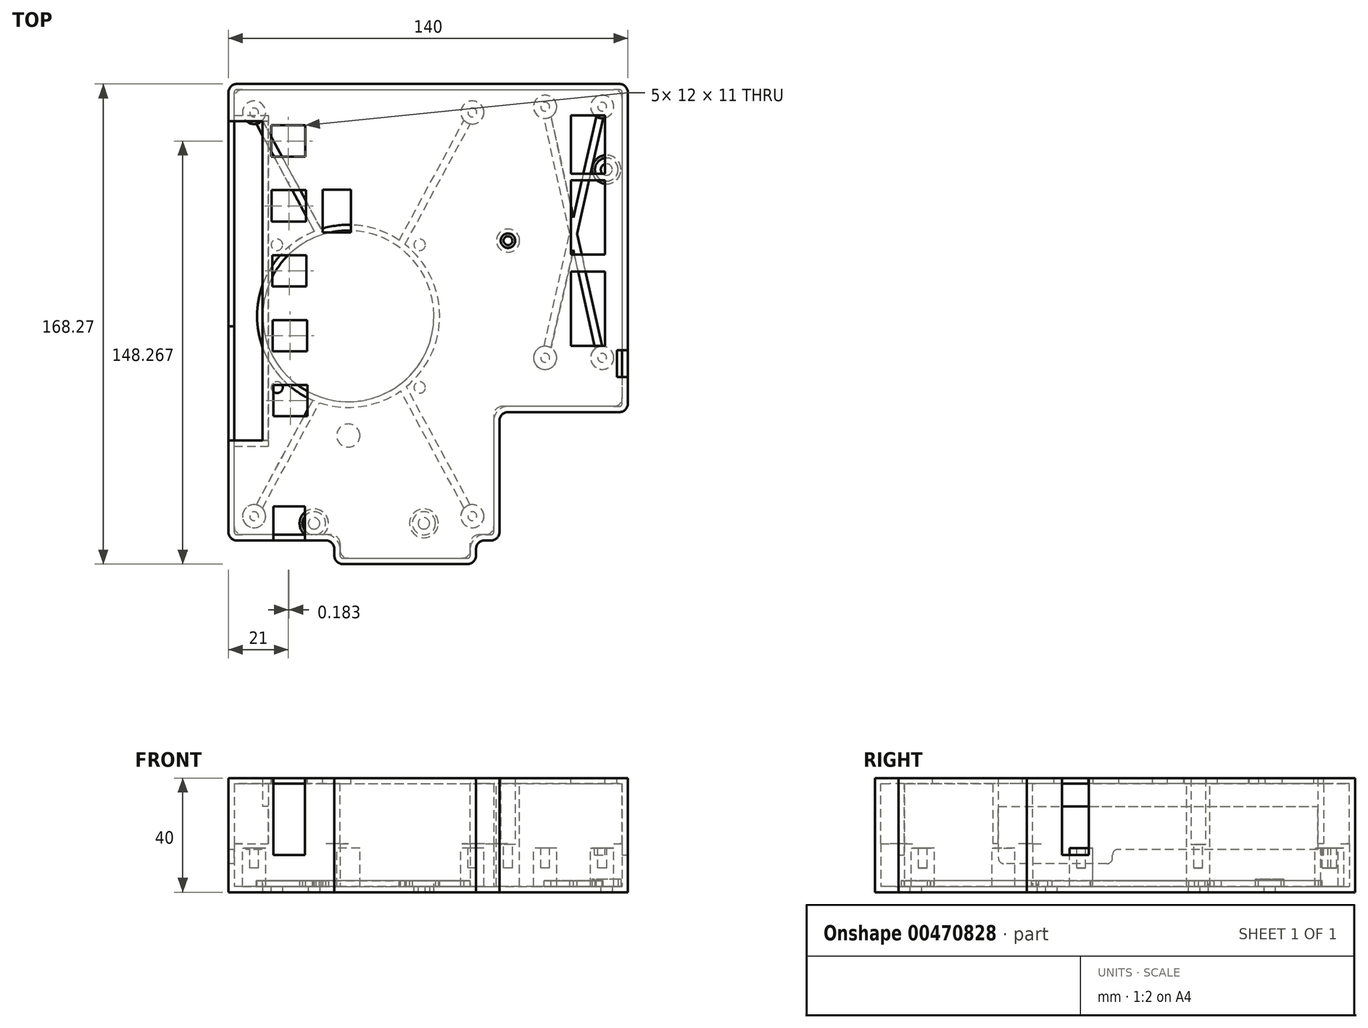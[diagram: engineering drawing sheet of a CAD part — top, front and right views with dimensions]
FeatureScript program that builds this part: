
annotation { "Feature Type Name" : "Feature", "Feature Type Description" : "" }
export const myFeature = defineFeature(function(context is Context, id is Id, definition is map)
    precondition{}
    {
        {
            assignVariable(context, id + "F0", {"name" : "BottomShellHeight", "anyValue" : 15 * mm});
        }
        {
            assignVariable(context, id + "F1", {"name" : "BoardThickness", "anyValue" : 1.6 * mm});
        }
        {
            assignVariable(context, id + "F2", {"name" : "TopShellHeight", "anyValue" : 23 * mm});
        }
        {
            var Q0;
            Q0=qCreatedBy(makeId("Top.planeOp"),FACE);
            var sketch = newSketch(context, id + "F3", { "sketchPlane" : qUnion([Q0])});
            skLineSegment(sketch, "E0", {"start": v(-42.03, -43.02) * mm, "end": v(-42.03, 116.98) * mm});
            skLineSegment(sketch, "E1", {"start": v(-42.03, 116.98) * mm, "end": v(97.97, 116.98) * mm});
            skLineSegment(sketch, "E2", {"start": v(97.97, 116.98) * mm, "end": v(97.97, 1.98) * mm});
            skLineSegment(sketch, "E3", {"start": v(97.97, 1.98) * mm, "end": v(52.97, 1.98) * mm});
            skLineSegment(sketch, "E4", {"start": v(52.97, 1.98) * mm, "end": v(52.97, -43.02) * mm});
            skLineSegment(sketch, "E5", {"start": v(52.97, -43.02) * mm, "end": v(-42.03, -43.02) * mm});
            skCircle(sketch, "E6", {"center": v(90.47, 86.98) * mm, "radius": 2.5 * mm});
            skCircle(sketch, "E7", {"center": v(90.47, 26.98) * mm, "radius": 2.5 * mm});
            skCircle(sketch, "E8", {"center": v(26.47, -37.02) * mm, "radius": 2.5 * mm});
            skCircle(sketch, "E9", {"center": v(-12.03, -37.02) * mm, "radius": 2.5 * mm});
            skLineSegment(sketch, "E10", {"start": v(-4.91, -43.02) * mm, "end": v(-4.91, -51.29) * mm});
            skLineSegment(sketch, "E11", {"start": v(-4.91, -51.29) * mm, "end": v(44.74, -51.29) * mm});
            skLineSegment(sketch, "E12", {"start": v(44.74, -51.29) * mm, "end": v(44.74, -43.02) * mm});
            skSolve(sketch);
        }
        {
            var Q0;
            Q0=makeQuery(id+"F3.imprint","IMPRINT",FACE,{"disambiguationData":[TD([[makeQuery(id+"F3.imprint","IMPRINT",EDGE,{"derivedFrom":sQuery(id+"F3.wireOp",EDGE,"E0")}),-1.0]])]});
            var Q1;
            Q1=makeQuery(id+"F3.imprint","IMPRINT",FACE,{"disambiguationData":[TD([[makeQuery(id+"F3.imprint","IMPRINT",EDGE,{"derivedFrom":sQuery(id+"F3.wireOp",EDGE,"E8")}),1.0]])]});
            var Q2;
            Q2=makeQuery(id+"F3.imprint","IMPRINT",FACE,{"disambiguationData":[TD([[makeQuery(id+"F3.imprint","IMPRINT",EDGE,{"derivedFrom":sQuery(id+"F3.wireOp",EDGE,"E9")}),1.0]])]});
            var Q3;
            Q3=makeQuery(id+"F3.imprint","IMPRINT",FACE,{"disambiguationData":[TD([[makeQuery(id+"F3.imprint","IMPRINT",EDGE,{"derivedFrom":sQuery(id+"F3.wireOp",EDGE,"E6")}),1.0]])]});
            var Q4;
            Q4=makeQuery(id+"F3.imprint","IMPRINT",FACE,{"disambiguationData":[TD([[makeQuery(id+"F3.imprint","IMPRINT",EDGE,{"derivedFrom":sQuery(id+"F3.wireOp",EDGE,"E7")}),1.0]])]});
            var Q5;
            {var subQ1=sQuery(id+"F3.wireOp",EDGE,"E10");Q5=makeQuery(id+"F3.imprint","IMPRINT",FACE,{"disambiguationData":[TD([[makeQuery(id+"F3.imprint","IMPRINT",EDGE,{"derivedFrom":subQ1}),1.0]])]});}
            extrude(context, id + "F4", {"entities" : qUnion([Q0, Q1, Q2, Q3, Q4, Q5]), "depth" : getVariable(context, 'BottomShellHeight')});
        }
        {
            var Q0;
            Q0=makeQuery(id+"F4.opExtrude","CAP_FACE",FACE,{"disambiguationData":[OSD([sQuery(id+"F3.wireOp",EDGE,"E0"),sQuery(id+"F3.wireOp",EDGE,"E1"),sQuery(id+"F3.wireOp",EDGE,"E2"),sQuery(id+"F3.wireOp",EDGE,"E3"),sQuery(id+"F3.wireOp",EDGE,"E4"),sQuery(id+"F3.wireOp",EDGE,"E5")])],"isStart":false});
            shell(context, id + "F5", {"entities" : qUnion([Q0]), "thickness" : 2 * mm});
        }
        {
            var Q0;
            Q0=sQuery(id+"F3.wireOp",VERTEX,"E9.center");
            var Q1;
            Q1=sQuery(id+"F3.wireOp",VERTEX,"E8.center");
            var Q2;
            Q2=sQuery(id+"F3.wireOp",VERTEX,"E6.center");
            var Q3;
            Q3=makeQuery(id+"F4.opExtrude","SWEPT_BODY",BODY,{"disambiguationData":[OSD([sQuery(id+"F3.wireOp",EDGE,"E0"),sQuery(id+"F3.wireOp",EDGE,"E1"),sQuery(id+"F3.wireOp",EDGE,"E2"),sQuery(id+"F3.wireOp",EDGE,"E3"),sQuery(id+"F3.wireOp",EDGE,"E4"),sQuery(id+"F3.wireOp",EDGE,"E5")])]});
            hole(context, id + "F6", {"style" : HoleStyle.SIMPLE, "holeDiameter" : 4 * mm, "endStyle" : HoleEndStyle.THROUGH, "oppositeDirection" : true, "locations" : qUnion([Q0, Q1, Q2]), "scope" : qUnion([Q3])});
        }
        {
            var Q0;
            Q0=makeQuery(id+"F5.opShell","OFFSET_FACE",FACE,{"disambiguationData":[OSD([sQuery(id+"F3.wireOp",EDGE,"E0"),sQuery(id+"F3.wireOp",EDGE,"E1"),sQuery(id+"F3.wireOp",EDGE,"E2"),sQuery(id+"F3.wireOp",EDGE,"E3"),sQuery(id+"F3.wireOp",EDGE,"E4"),sQuery(id+"F3.wireOp",EDGE,"E5")])]});
            var sketch = newSketch(context, id + "F7", { "sketchPlane" : qUnion([Q0])});
            skCircle(sketch, "E13", {"center": v(-12.03, -37.02) * mm, "radius": 4.05 * mm});
            skCircle(sketch, "E14", {"center": v(26.47, -37.02) * mm, "radius": 4.05 * mm});
            skCircle(sketch, "E15", {"center": v(90.47, 86.98) * mm, "radius": 4.05 * mm});
            skCircle(sketch, "E16", {"center": v(90.47, 86.98) * mm, "radius": 5.05 * mm});
            skCircle(sketch, "E17", {"center": v(26.47, -37.02) * mm, "radius": 5.05 * mm});
            skCircle(sketch, "E18", {"center": v(-12.03, -37.02) * mm, "radius": 5.05 * mm});
            skLineSegment(sketch, "E19.rect.bottom", {"start": v(25, 10.6) * mm, "end": v(-25, 10.6) * mm, "construction": true});
            skLineSegment(sketch, "E19.rect.top", {"start": v(25, 60.6) * mm, "end": v(-25, 60.6) * mm, "construction": true});
            skLineSegment(sketch, "E19.rect.left", {"start": v(25, 10.6) * mm, "end": v(25, 60.6) * mm, "construction": true});
            skLineSegment(sketch, "E19.rect.right", {"start": v(-25, 10.6) * mm, "end": v(-25, 60.6) * mm, "construction": true});
            skPoint(sketch, "E19.rect.middle", {"position": v(0, 35.6) * mm});
            skCircle(sketch, "E20", {"center": v(0, 35.6) * mm, "radius": 30 * mm});
            skSolve(sketch);
        }
        {
            var Q0;
            Q0=makeQuery(id+"F7.imprint","IMPRINT",FACE,{"disambiguationData":[TD([[makeQuery(id+"F7.imprint","IMPRINT",EDGE,{"derivedFrom":sQuery(id+"F7.wireOp",EDGE,"E15")}),-1.0]])]});
            extrude(context, id + "F8", {"entities" : qUnion([Q0]), "operationType" : NewBodyOperationType.ADD, "depth" : 2.5 * mm});
        }
        {
            var Q0;
            Q0=makeQuery(id+"F7.imprint","IMPRINT",FACE,{"disambiguationData":[TD([[makeQuery(id+"F7.imprint","IMPRINT",EDGE,{"derivedFrom":sQuery(id+"F7.wireOp",EDGE,"E16")}),-1.0]])]});
            cPlane(context, id + "F9", {"entities" : qUnion([Q0]), "cplaneType" : CPlaneType.OFFSET, "offset" : getVariable(context, 'BottomShellHeight') - getVariable(context, 'BoardThickness'), "width" : 150 * mm, "height" : 150 * mm});
        }
        {
            var Q0;
            Q0=qCreatedBy(id+"F9.planeOp",FACE);
            var sketch = newSketch(context, id + "F10", { "sketchPlane" : qUnion([Q0])});
            skCircle(sketch, "E21", {"center": v(-33.03, 106.98) * mm, "radius": 4.05 * mm});
            skCircle(sketch, "E22", {"center": v(43.47, 106.98) * mm, "radius": 4.05 * mm});
            skCircle(sketch, "E23", {"center": v(68.97, 108.98) * mm, "radius": 4.05 * mm});
            skCircle(sketch, "E24", {"center": v(88.97, 108.98) * mm, "radius": 4.05 * mm});
            skCircle(sketch, "E25", {"center": v(68.97, 20.98) * mm, "radius": 4.05 * mm});
            skCircle(sketch, "E26", {"center": v(-33.03, -34.52) * mm, "radius": 4.05 * mm});
            skCircle(sketch, "E27", {"center": v(43.47, -34.52) * mm, "radius": 4.05 * mm});
            skCircle(sketch, "E28", {"center": v(88.97, 20.98) * mm, "radius": 4.05 * mm});
            skCircle(sketch, "E29", {"center": v(0, -6.24) * mm, "radius": 4.05 * mm});
            skCircle(sketch, "E30", {"center": v(55.94, 62.04) * mm, "radius": 4.05 * mm});
            skSolve(sketch);
        }
        {
            var Q0;
            Q0=qSketchRegion(id+"F10",true);
            extrude(context, id + "F11", {"entities" : qUnion([Q0]), "operationType" : NewBodyOperationType.ADD, "endBound" : BoundingType.UP_TO_NEXT, "oppositeDirection" : true, "depth" : 25 * mm});
        }
        {
            var Q0;
            Q0=qCreatedBy(makeId("Top.planeOp"),FACE);
            cPlane(context, id + "F12", {"entities" : qUnion([Q0]), "cplaneType" : CPlaneType.OFFSET, "offset" : 4 * mm, "width" : 150 * mm, "height" : 150 * mm});
        }
        {
            var Q0;
            Q0=qCreatedBy(id+"F12.planeOp",FACE);
            var sketch = newSketch(context, id + "F13", { "sketchPlane" : qUnion([Q0])});
            skCircle(sketch, "E31.0", {"center": v(-33.03, 106.98) * mm, "radius": 4.05 * mm, "construction": true});
            skCircle(sketch, "E31.1", {"center": v(43.47, 106.98) * mm, "radius": 4.05 * mm, "construction": true});
            skCircle(sketch, "E31.2", {"center": v(68.97, 108.98) * mm, "radius": 4.05 * mm, "construction": true});
            skCircle(sketch, "E31.3", {"center": v(88.97, 108.98) * mm, "radius": 4.05 * mm, "construction": true});
            skCircle(sketch, "E31.5", {"center": v(68.97, 20.98) * mm, "radius": 4.05 * mm, "construction": true});
            skCircle(sketch, "E31.6", {"center": v(43.47, -34.52) * mm, "radius": 4.05 * mm, "construction": true});
            skCircle(sketch, "E31.7", {"center": v(-33.03, -34.52) * mm, "radius": 4.05 * mm, "construction": true});
            skLineSegment(sketch, "E32", {"start": v(-33.03, 106.98) * mm, "end": v(43.47, -34.52) * mm, "construction": true});
            skLineSegment(sketch, "E33", {"start": v(68.97, 108.98) * mm, "end": v(88.97, 18.98) * mm, "construction": true});
            skLineSegment(sketch, "E34", {"start": v(88.97, 108.98) * mm, "end": v(68.97, 20.98) * mm, "construction": true});
            skLineSegment(sketch, "E35", {"start": v(43.47, 106.98) * mm, "end": v(-33.03, -34.52) * mm, "construction": true});
            skArc(sketch, "E36.0.startCap", {"start": v(-34.13, 106.38) * mm, "mid": v(-33.62, 108.08) * mm, "end": v(-31.93, 107.57) * mm});
            skArc(sketch, "E36.0.endCap", {"start": v(44.57, -33.93) * mm, "mid": v(44.06, -35.62) * mm, "end": v(42.37, -35.12) * mm});
            skLineSegment(sketch, "E36.0.left", {"start": v(-31.93, 107.57) * mm, "end": v(44.57, -33.93) * mm});
            skLineSegment(sketch, "E36.0.right", {"start": v(-34.13, 106.38) * mm, "end": v(42.37, -35.12) * mm});
            skArc(sketch, "E36.1.startCap", {"start": v(42.37, 107.57) * mm, "mid": v(44.06, 108.08) * mm, "end": v(44.57, 106.38) * mm});
            skArc(sketch, "E36.1.endCap", {"start": v(-31.93, -35.12) * mm, "mid": v(-33.62, -35.62) * mm, "end": v(-34.13, -33.93) * mm});
            skLineSegment(sketch, "E36.1.left", {"start": v(44.57, 106.38) * mm, "end": v(-31.93, -35.12) * mm});
            skLineSegment(sketch, "E36.1.right", {"start": v(42.37, 107.57) * mm, "end": v(-34.13, -33.93) * mm});
            skArc(sketch, "E36.2.startCap", {"start": v(42.27, 106.64) * mm, "mid": v(43.13, 108.18) * mm, "end": v(44.67, 107.32) * mm});
            skArc(sketch, "E36.2.endCap", {"start": v(70.17, 21.32) * mm, "mid": v(69.3, 19.77) * mm, "end": v(67.77, 20.64) * mm});
            skArc(sketch, "E36.3.startCap", {"start": v(44.7, -34.74) * mm, "mid": v(43.25, -35.75) * mm, "end": v(42.24, -34.3) * mm});
            skArc(sketch, "E36.3.endCap", {"start": v(67.74, 109.2) * mm, "mid": v(69.19, 110.2) * mm, "end": v(70.2, 108.76) * mm});
            skArc(sketch, "E36.4.startCap", {"start": v(67.75, 108.7) * mm, "mid": v(68.7, 110.2) * mm, "end": v(70.2, 109.25) * mm});
            skArc(sketch, "E36.4.endCap", {"start": v(90.2, 19.25) * mm, "mid": v(89.24, 17.76) * mm, "end": v(87.75, 18.7) * mm});
            skLineSegment(sketch, "E36.4.left", {"start": v(70.2, 109.25) * mm, "end": v(90.2, 19.25) * mm});
            skLineSegment(sketch, "E36.4.right", {"start": v(67.75, 108.7) * mm, "end": v(87.75, 18.7) * mm});
            skArc(sketch, "E36.5.startCap", {"start": v(87.75, 109.25) * mm, "mid": v(89.25, 110.2) * mm, "end": v(90.19, 108.7) * mm});
            skArc(sketch, "E36.5.endCap", {"start": v(70.19, 20.7) * mm, "mid": v(68.7, 19.76) * mm, "end": v(67.75, 21.25) * mm});
            skLineSegment(sketch, "E36.5.left", {"start": v(90.19, 108.7) * mm, "end": v(70.19, 20.7) * mm});
            skLineSegment(sketch, "E36.5.right", {"start": v(87.75, 109.25) * mm, "end": v(67.75, 21.25) * mm});
            skCircle(sketch, "E37.0", {"center": v(88.97, 20.98) * mm, "radius": 4.05 * mm});
            skCircle(sketch, "E38.0", {"center": v(0, 35.6) * mm, "radius": 32 * mm});
            skSolve(sketch);
        }
        {
            var Q0;
            Q0=qSketchRegion(id+"F13",true);
            var Q1;
            Q1=makeQuery(id+"F5.opShell","OFFSET_FACE",FACE,{"disambiguationData":[OSD([sQuery(id+"F3.wireOp",EDGE,"E0"),sQuery(id+"F3.wireOp",EDGE,"E1"),sQuery(id+"F3.wireOp",EDGE,"E2"),sQuery(id+"F3.wireOp",EDGE,"E3"),sQuery(id+"F3.wireOp",EDGE,"E4"),sQuery(id+"F3.wireOp",EDGE,"E5")])]});
            extrude(context, id + "F14", {"entities" : qUnion([Q0]), "operationType" : NewBodyOperationType.ADD, "endBound" : BoundingType.UP_TO_SURFACE, "oppositeDirection" : true, "endBoundEntityFace" : qUnion([Q1]), "depth" : 25 * mm});
        }
        {
            var Q0;
            Q0=makeQuery(id+"F7.imprint","IMPRINT",FACE,{"disambiguationData":[TD([[makeQuery(id+"F7.imprint","IMPRINT",EDGE,{"derivedFrom":sQuery(id+"F7.wireOp",EDGE,"E20")}),1.0]])]});
            extrude(context, id + "F15", {"entities" : qUnion([Q0]), "operationType" : NewBodyOperationType.REMOVE, "endBound" : BoundingType.SYMMETRIC, "oppositeDirection" : true, "depth" : 5 * mm});
        }
        {
            var Q0;
            Q0=makeQuery(id+"F4.opExtrude","SWEPT_EDGE",EDGE,{"disambiguationData":[OSD([sQuery(id+"F3.wireOp",EDGE,"E0"),sQuery(id+"F3.wireOp",EDGE,"E5")])]});
            var Q1;
            Q1=makeQuery(id+"F4.opExtrude","SWEPT_EDGE",EDGE,{"disambiguationData":[OSD([sQuery(id+"F3.wireOp",EDGE,"E4"),sQuery(id+"F3.wireOp",EDGE,"E5")])]});
            var Q2;
            Q2=makeQuery(id+"F4.opExtrude","SWEPT_EDGE",EDGE,{"disambiguationData":[OSD([sQuery(id+"F3.wireOp",EDGE,"E3"),sQuery(id+"F3.wireOp",EDGE,"E4")])]});
            var Q3;
            Q3=makeQuery(id+"F4.opExtrude","SWEPT_EDGE",EDGE,{"disambiguationData":[OSD([sQuery(id+"F3.wireOp",EDGE,"E2"),sQuery(id+"F3.wireOp",EDGE,"E3")])]});
            var Q4;
            Q4=makeQuery(id+"F4.opExtrude","SWEPT_EDGE",EDGE,{"disambiguationData":[OSD([sQuery(id+"F3.wireOp",EDGE,"E1"),sQuery(id+"F3.wireOp",EDGE,"E2")])]});
            var Q5;
            Q5=makeQuery(id+"F4.opExtrude","SWEPT_EDGE",EDGE,{"disambiguationData":[OSD([sQuery(id+"F3.wireOp",EDGE,"E0"),sQuery(id+"F3.wireOp",EDGE,"E1")])]});
            var Q6;
            Q6=makeQuery(id+"F5.opShell","OFFSET_EDGE",EDGE,{"disambiguationData":[OSD([sQuery(id+"F3.wireOp",EDGE,"E0"),sQuery(id+"F3.wireOp",EDGE,"E5")])]});
            var Q7;
            Q7=makeQuery(id+"F5.opShell","OFFSET_EDGE",EDGE,{"disambiguationData":[OSD([sQuery(id+"F3.wireOp",EDGE,"E0"),sQuery(id+"F3.wireOp",EDGE,"E1")])]});
            var Q8;
            Q8=makeQuery(id+"F5.opShell","OFFSET_EDGE",EDGE,{"disambiguationData":[OSD([sQuery(id+"F3.wireOp",EDGE,"E1"),sQuery(id+"F3.wireOp",EDGE,"E2")])]});
            var Q9;
            Q9=makeQuery(id+"F5.opShell","OFFSET_EDGE",EDGE,{"disambiguationData":[OSD([sQuery(id+"F3.wireOp",EDGE,"E4"),sQuery(id+"F3.wireOp",EDGE,"E5")])]});
            var Q10;
            Q10=makeQuery(id+"F5.opShell","OFFSET_EDGE",EDGE,{"disambiguationData":[OSD([sQuery(id+"F3.wireOp",EDGE,"E3"),sQuery(id+"F3.wireOp",EDGE,"E4")])]});
            var Q11;
            Q11=makeQuery(id+"F5.opShell","OFFSET_EDGE",EDGE,{"disambiguationData":[OSD([sQuery(id+"F3.wireOp",EDGE,"E2"),sQuery(id+"F3.wireOp",EDGE,"E3")])]});
            var Q12;
            Q12=makeQuery(id+"F4.opExtrude","SWEPT_EDGE",EDGE,{"disambiguationData":[OSD([sQuery(id+"F3.wireOp",EDGE,"E10"),sQuery(id+"F3.wireOp",EDGE,"E11")])]});
            var Q13;
            Q13=makeQuery(id+"F4.opExtrude","SWEPT_EDGE",EDGE,{"disambiguationData":[OSD([sQuery(id+"F3.wireOp",EDGE,"E11"),sQuery(id+"F3.wireOp",EDGE,"E12")])]});
            var Q14;
            Q14=makeQuery(id+"F5.opShell","OFFSET_EDGE",EDGE,{"disambiguationData":[OSD([sQuery(id+"F3.wireOp",EDGE,"E10"),sQuery(id+"F3.wireOp",EDGE,"E11")])]});
            var Q15;
            Q15=makeQuery(id+"F5.opShell","OFFSET_EDGE",EDGE,{"disambiguationData":[OSD([sQuery(id+"F3.wireOp",EDGE,"E5"),sQuery(id+"F3.wireOp",EDGE,"E10")])]});
            var Q16;
            Q16=makeQuery(id+"F5.opShell","OFFSET_EDGE",EDGE,{"disambiguationData":[OSD([sQuery(id+"F3.wireOp",EDGE,"E5"),sQuery(id+"F3.wireOp",EDGE,"E12")])]});
            var Q17;
            Q17=makeQuery(id+"F5.opShell","OFFSET_EDGE",EDGE,{"disambiguationData":[OSD([sQuery(id+"F3.wireOp",EDGE,"E11"),sQuery(id+"F3.wireOp",EDGE,"E12")])]});
            var Q18;
            Q18=makeQuery(id+"F4.opExtrude","SWEPT_EDGE",EDGE,{"disambiguationData":[OSD([sQuery(id+"F3.wireOp",EDGE,"E5"),sQuery(id+"F3.wireOp",EDGE,"E12")])]});
            var Q19;
            Q19=makeQuery(id+"F4.opExtrude","SWEPT_EDGE",EDGE,{"disambiguationData":[OSD([sQuery(id+"F3.wireOp",EDGE,"E5"),sQuery(id+"F3.wireOp",EDGE,"E10")])]});
            fillet(context, id + "F16", {"entities" : qUnion([Q0, Q1, Q2, Q3, Q4, Q5, Q6, Q7, Q8, Q9, Q10, Q11, Q12, Q13, Q14, Q15, Q16, Q17, Q18, Q19]), "radius" : 3 * mm, "tangentPropagation" : true, "allowEdgeOverflow" : false});
        }
        {
            var Q0;
            Q0=makeQuery(id+"F11.opExtrude","CAP_FACE",FACE,{"disambiguationData":[OSD([sQuery(id+"F10.wireOp",EDGE,"E27")])],"isStart":true});
            var sketch = newSketch(context, id + "F17", { "sketchPlane" : qUnion([Q0])});
            skCircle(sketch, "E39.0", {"center": v(-33.03, -34.52) * mm, "radius": 4.05 * mm, "construction": true});
            skCircle(sketch, "E39.1", {"center": v(-33.03, 106.98) * mm, "radius": 4.05 * mm, "construction": true});
            skCircle(sketch, "E39.2", {"center": v(43.47, 106.98) * mm, "radius": 4.05 * mm, "construction": true});
            skCircle(sketch, "E39.3", {"center": v(43.47, -34.52) * mm, "radius": 4.05 * mm, "construction": true});
            skCircle(sketch, "E39.4", {"center": v(68.97, 20.98) * mm, "radius": 4.05 * mm, "construction": true});
            skCircle(sketch, "E39.5", {"center": v(68.97, 108.98) * mm, "radius": 4.05 * mm, "construction": true});
            skCircle(sketch, "E39.7", {"center": v(88.97, 108.98) * mm, "radius": 4.05 * mm, "construction": true});
            skCircle(sketch, "E40", {"center": v(-33.03, -34.52) * mm, "radius": 1.55 * mm});
            skCircle(sketch, "E41", {"center": v(43.47, -34.52) * mm, "radius": 1.55 * mm});
            skCircle(sketch, "E42", {"center": v(-33.03, 106.98) * mm, "radius": 1.55 * mm});
            skCircle(sketch, "E43", {"center": v(43.47, 106.98) * mm, "radius": 1.55 * mm});
            skCircle(sketch, "E44", {"center": v(68.97, 20.98) * mm, "radius": 1.55 * mm});
            skCircle(sketch, "E45", {"center": v(68.97, 108.98) * mm, "radius": 1.55 * mm});
            skCircle(sketch, "E46", {"center": v(88.97, 108.98) * mm, "radius": 1.55 * mm});
            skCircle(sketch, "E47.0", {"center": v(88.97, 20.98) * mm, "radius": 4.05 * mm});
            skCircle(sketch, "E48", {"center": v(88.97, 20.98) * mm, "radius": 1.55 * mm});
            skCircle(sketch, "E49.0.0", {"center": v(55.94, 62.04) * mm, "radius": 4.05 * mm});
            skCircle(sketch, "E50", {"center": v(55.94, 62.04) * mm, "radius": 1.55 * mm});
            skSolve(sketch);
        }
        {
            var Q0;
            Q0=makeQuery(id+"F17.imprint","IMPRINT",FACE,{"disambiguationData":[TD([[makeQuery(id+"F17.imprint","IMPRINT",EDGE,{"derivedFrom":sQuery(id+"F17.wireOp",EDGE,"E48")}),1.0]])]});
            var Q1;
            Q1=makeQuery(id+"F17.imprint","IMPRINT",FACE,{"disambiguationData":[TD([[makeQuery(id+"F17.imprint","IMPRINT",EDGE,{"derivedFrom":sQuery(id+"F17.wireOp",EDGE,"E44")}),1.0]])]});
            var Q2;
            Q2=makeQuery(id+"F17.imprint","IMPRINT",FACE,{"disambiguationData":[TD([[makeQuery(id+"F17.imprint","IMPRINT",EDGE,{"derivedFrom":sQuery(id+"F17.wireOp",EDGE,"E41")}),1.0]])]});
            var Q3;
            Q3=makeQuery(id+"F17.imprint","IMPRINT",FACE,{"disambiguationData":[TD([[makeQuery(id+"F17.imprint","IMPRINT",EDGE,{"derivedFrom":sQuery(id+"F17.wireOp",EDGE,"E40")}),1.0]])]});
            var Q4;
            Q4=makeQuery(id+"F17.imprint","IMPRINT",FACE,{"disambiguationData":[TD([[makeQuery(id+"F17.imprint","IMPRINT",EDGE,{"derivedFrom":sQuery(id+"F17.wireOp",EDGE,"E42")}),1.0]])]});
            var Q5;
            Q5=makeQuery(id+"F17.imprint","IMPRINT",FACE,{"disambiguationData":[TD([[makeQuery(id+"F17.imprint","IMPRINT",EDGE,{"derivedFrom":sQuery(id+"F17.wireOp",EDGE,"E43")}),1.0]])]});
            var Q6;
            Q6=makeQuery(id+"F17.imprint","IMPRINT",FACE,{"disambiguationData":[TD([[makeQuery(id+"F17.imprint","IMPRINT",EDGE,{"derivedFrom":sQuery(id+"F17.wireOp",EDGE,"E45")}),1.0]])]});
            var Q7;
            Q7=makeQuery(id+"F17.imprint","IMPRINT",FACE,{"disambiguationData":[TD([[makeQuery(id+"F17.imprint","IMPRINT",EDGE,{"derivedFrom":sQuery(id+"F17.wireOp",EDGE,"E46")}),1.0]])]});
            var Q8;
            Q8=makeQuery(id+"F17.imprint","IMPRINT",FACE,{"disambiguationData":[TD([[makeQuery(id+"F17.imprint","IMPRINT",EDGE,{"derivedFrom":sQuery(id+"F17.wireOp",EDGE,"E50")}),1.0]])]});
            extrude(context, id + "F18", {"entities" : qUnion([Q0, Q1, Q2, Q3, Q4, Q5, Q6, Q7, Q8]), "operationType" : NewBodyOperationType.REMOVE, "oppositeDirection" : true, "depth" : 7 * mm});
        }
        {
            var Q0;
            {var subQ0=sQuery(id+"F3.wireOp",EDGE,"E2");var subQ1=sQuery(id+"F3.wireOp",EDGE,"E3");var subQ2=sQuery(id+"F3.wireOp",EDGE,"E4");var subQ3=sQuery(id+"F3.wireOp",EDGE,"E5");Q0=makeQuery(id+"FDKzRyLnrHQ0L6F_1.boolean.opBoolean","SPLIT",FACE,{"disambiguationData":[TD([makeQuery(id+"F4.opExtrude","SWEPT_FACE",FACE,{"disambiguationData":[OSD([subQ1])]})])],"derivedFrom":makeQuery(id+"F4.opExtrude","CAP_FACE",FACE,{"disambiguationData":[OSD([sQuery(id+"F3.wireOp",EDGE,"E0"),sQuery(id+"F3.wireOp",EDGE,"E1"),subQ0,subQ1,subQ2,subQ3])],"isStart":false})});}
            var sketch = newSketch(context, id + "F19", { "sketchPlane" : qUnion([Q0])});
            skArc(sketch, "E51.0", {"start": v(-41.03, -40.02) * mm, "mid": v(-40.44, -41.44) * mm, "end": v(-39.03, -42.02) * mm});
            skLineSegment(sketch, "E51.1", {"start": v(-7.91, -42.02) * mm, "end": v(-39.03, -42.02) * mm});
            skArc(sketch, "E51.2", {"start": v(-7.91, -42.02) * mm, "mid": v(-5.08, -43.2) * mm, "end": v(-3.91, -46.02) * mm});
            skLineSegment(sketch, "E51.3", {"start": v(-3.91, -46.02) * mm, "end": v(-3.91, -48.29) * mm});
            skArc(sketch, "E51.4", {"start": v(-3.91, -48.29) * mm, "mid": v(-3.33, -49.7) * mm, "end": v(-1.91, -50.29) * mm});
            skLineSegment(sketch, "E51.5", {"start": v(-41.03, -40.02) * mm, "end": v(-41.03, 113.98) * mm});
            skLineSegment(sketch, "E51.6", {"start": v(-1.91, -50.29) * mm, "end": v(41.74, -50.29) * mm});
            skArc(sketch, "E51.7", {"start": v(41.74, -50.29) * mm, "mid": v(43.15, -49.7) * mm, "end": v(43.74, -48.29) * mm});
            skLineSegment(sketch, "E51.8", {"start": v(43.74, -48.29) * mm, "end": v(43.74, -46.02) * mm});
            skArc(sketch, "E51.9", {"start": v(43.74, -46.02) * mm, "mid": v(44.9, -43.2) * mm, "end": v(47.74, -42.02) * mm});
            skLineSegment(sketch, "E51.10", {"start": v(96.97, 113.98) * mm, "end": v(96.97, 4.98) * mm});
            skArc(sketch, "E51.11", {"start": v(96.97, 113.98) * mm, "mid": v(96.38, 115.4) * mm, "end": v(94.97, 115.98) * mm});
            skLineSegment(sketch, "E51.12", {"start": v(-39.03, 115.98) * mm, "end": v(94.97, 115.98) * mm});
            skArc(sketch, "E51.13", {"start": v(-39.03, 115.98) * mm, "mid": v(-40.44, 115.4) * mm, "end": v(-41.03, 113.98) * mm});
            skArc(sketch, "E51.14", {"start": v(94.97, 2.98) * mm, "mid": v(96.38, 3.56) * mm, "end": v(96.97, 4.98) * mm});
            skLineSegment(sketch, "E51.15", {"start": v(94.97, 2.98) * mm, "end": v(55.97, 2.98) * mm});
            skArc(sketch, "E51.16", {"start": v(51.97, -1.02) * mm, "mid": v(53.14, 1.8) * mm, "end": v(55.97, 2.98) * mm});
            skLineSegment(sketch, "E51.17", {"start": v(51.97, -1.02) * mm, "end": v(51.97, -40.02) * mm});
            skArc(sketch, "E51.18", {"start": v(49.97, -42.02) * mm, "mid": v(51.38, -41.44) * mm, "end": v(51.97, -40.02) * mm});
            skLineSegment(sketch, "E51.19", {"start": v(49.97, -42.02) * mm, "end": v(47.74, -42.02) * mm});
            skSolve(sketch);
        }
        {
            var Q0;
            Q0=makeQuery(id+"F19.imprint","IMPRINT",FACE,{"disambiguationData":[TD([[makeQuery(id+"F19.imprint","IMPRINT",EDGE,{"derivedFrom":sQuery(id+"F19.wireOp",EDGE,"E51.0")}),-1.0]])]});
            extrude(context, id + "F20", {"entities" : qUnion([Q0]), "operationType" : NewBodyOperationType.ADD, "depth" : 2 * mm});
        }
        {
            var Q0;
            Q0=makeQuery(id+"F4.opExtrude","CAP_FACE",FACE,{"disambiguationData":[OSD([sQuery(id+"F3.wireOp",EDGE,"E0"),sQuery(id+"F3.wireOp",EDGE,"E1"),sQuery(id+"F3.wireOp",EDGE,"E2"),sQuery(id+"F3.wireOp",EDGE,"E3"),sQuery(id+"F3.wireOp",EDGE,"E4"),sQuery(id+"F3.wireOp",EDGE,"E5")])],"isStart":false});
            extrude(context, id + "F21", {"entities" : qUnion([Q0]), "depth" : 2 * mm});
        }
        {
            var Q0;
            Q0=makeQuery(id+"F20.opExtrude","CAP_FACE",FACE,{"disambiguationData":[OSD([sQuery(id+"F3.wireOp",EDGE,"E0"),sQuery(id+"F3.wireOp",EDGE,"E1"),sQuery(id+"F3.wireOp",EDGE,"E2"),sQuery(id+"F3.wireOp",EDGE,"E3"),sQuery(id+"F3.wireOp",EDGE,"E4"),sQuery(id+"F3.wireOp",EDGE,"E5"),sQuery(id+"F19.wireOp",EDGE,"82df2995-c3c6-4384-91ae-508e72de70b8.0"),sQuery(id+"F19.wireOp",EDGE,"82df2995-c3c6-4384-91ae-508e72de70b8.1"),sQuery(id+"F19.wireOp",EDGE,"82df2995-c3c6-4384-91ae-508e72de70b8.2"),sQuery(id+"F19.wireOp",EDGE,"82df2995-c3c6-4384-91ae-508e72de70b8.3"),sQuery(id+"F19.wireOp",EDGE,"82df2995-c3c6-4384-91ae-508e72de70b8.4"),sQuery(id+"F19.wireOp",EDGE,"82df2995-c3c6-4384-91ae-508e72de70b8.5"),sQuery(id+"F19.wireOp",EDGE,"82df2995-c3c6-4384-91ae-508e72de70b8.6"),sQuery(id+"F19.wireOp",EDGE,"82df2995-c3c6-4384-91ae-508e72de70b8.7"),sQuery(id+"F19.wireOp",EDGE,"82df2995-c3c6-4384-91ae-508e72de70b8.8"),sQuery(id+"F19.wireOp",EDGE,"befe2b45-20a4-4501-920e-873b11abf4d8.0"),sQuery(id+"F19.wireOp",EDGE,"befe2b45-20a4-4501-920e-873b11abf4d8.1"),sQuery(id+"F19.wireOp",EDGE,"befe2b45-20a4-4501-920e-873b11abf4d8.2")])],"isStart":false});
            var sketch = newSketch(context, id + "F22", { "sketchPlane" : qUnion([Q0])});
            skArc(sketch, "E52.0", {"start": v(-39.03, 116.98) * mm, "mid": v(-41.15, 116.1) * mm, "end": v(-42.03, 113.98) * mm});
            skLineSegment(sketch, "E52.1", {"start": v(-39.03, 116.98) * mm, "end": v(94.97, 116.98) * mm});
            skLineSegment(sketch, "E52.2", {"start": v(-42.03, -40.02) * mm, "end": v(-42.03, -8.02) * mm});
            skArc(sketch, "E52.3", {"start": v(-42.03, -40.02) * mm, "mid": v(-41.15, -42.14) * mm, "end": v(-39.03, -43.02) * mm});
            skArc(sketch, "E52.5", {"start": v(49.97, -43.02) * mm, "mid": v(52.1, -42.14) * mm, "end": v(52.97, -40.02) * mm});
            skLineSegment(sketch, "E52.6", {"start": v(52.97, -1.02) * mm, "end": v(52.97, -40.02) * mm});
            skArc(sketch, "E52.7", {"start": v(52.97, -1.02) * mm, "mid": v(53.85, 1.1) * mm, "end": v(55.97, 1.98) * mm});
            skLineSegment(sketch, "E52.8", {"start": v(94.97, 1.98) * mm, "end": v(55.97, 1.98) * mm});
            skArc(sketch, "E52.9", {"start": v(94.97, 1.98) * mm, "mid": v(97.1, 2.86) * mm, "end": v(97.97, 4.98) * mm});
            skLineSegment(sketch, "E52.10", {"start": v(97.97, 113.98) * mm, "end": v(97.97, 4.98) * mm});
            skArc(sketch, "E52.11", {"start": v(97.97, 113.98) * mm, "mid": v(97.1, 116.1) * mm, "end": v(94.97, 116.98) * mm});
            skLineSegment(sketch, "E53.0", {"start": v(-7.91, -43.02) * mm, "end": v(-39.03, -43.02) * mm});
            skArc(sketch, "E53.1", {"start": v(-7.91, -43.02) * mm, "mid": v(-5.8, -43.9) * mm, "end": v(-4.91, -46.02) * mm});
            skLineSegment(sketch, "E53.2", {"start": v(-4.91, -46.02) * mm, "end": v(-4.91, -48.29) * mm});
            skArc(sketch, "E53.3", {"start": v(-4.91, -48.29) * mm, "mid": v(-4.03, -50.4) * mm, "end": v(-1.91, -51.29) * mm});
            skLineSegment(sketch, "E53.4", {"start": v(-1.91, -51.29) * mm, "end": v(41.74, -51.29) * mm});
            skArc(sketch, "E53.5", {"start": v(41.74, -51.29) * mm, "mid": v(43.86, -50.4) * mm, "end": v(44.74, -48.29) * mm});
            skLineSegment(sketch, "E53.6", {"start": v(44.74, -48.29) * mm, "end": v(44.74, -46.02) * mm});
            skArc(sketch, "E53.7", {"start": v(44.74, -46.02) * mm, "mid": v(45.62, -43.9) * mm, "end": v(47.74, -43.02) * mm});
            skLineSegment(sketch, "E53.8", {"start": v(49.97, -43.02) * mm, "end": v(47.74, -43.02) * mm});
            skLineSegment(sketch, "E54.bottom", {"start": v(-42.03, 103.98) * mm, "end": v(-30.03, 103.98) * mm});
            skLineSegment(sketch, "E54.top", {"start": v(-42.03, -8.02) * mm, "end": v(-30.03, -8.02) * mm});
            skLineSegment(sketch, "E54.left", {"start": v(-42.03, 103.98) * mm, "end": v(-42.03, 103.98) * mm});
            skLineSegment(sketch, "E54.right", {"start": v(-30.03, 103.98) * mm, "end": v(-30.03, -8.02) * mm});
            skLineSegment(sketch, "E55", {"start": v(-42.03, -8.02) * mm, "end": v(-42.03, -8.02) * mm});
            skLineSegment(sketch, "E56", {"start": v(-42.03, 103.98) * mm, "end": v(-42.03, 113.98) * mm});
            skSolve(sketch);
        }
        {
            var Q0;
            Q0=qSketchRegion(id+"F22",true);
            extrude(context, id + "F23", {"entities" : qUnion([Q0]), "operationType" : NewBodyOperationType.ADD, "depth" : getVariable(context, 'TopShellHeight')});
        }
        {
            var Q0;
            {var subQ5=sQuery(id+"F3.wireOp",EDGE,"E0");Q0=makeQuery(id+"F23.boolean.opBoolean","SPLIT",FACE,{"disambiguationData":[TD([makeQuery(id+"F21.opExtrude","SWEPT_FACE",FACE,{"disambiguationData":[OSD([subQ5])]})])],"derivedFrom":makeQuery(id+"F23.opExtrude","CAP_FACE",FACE,{"disambiguationData":[OSD([sQuery(id+"F22.wireOp",EDGE,"E52.0"),sQuery(id+"F22.wireOp",EDGE,"E52.1"),sQuery(id+"F22.wireOp",EDGE,"E52.2"),sQuery(id+"F22.wireOp",EDGE,"E52.3"),sQuery(id+"F22.wireOp",EDGE,"E52.4"),sQuery(id+"F22.wireOp",EDGE,"E52.5"),sQuery(id+"F22.wireOp",EDGE,"E52.6"),sQuery(id+"F22.wireOp",EDGE,"E52.7"),sQuery(id+"F22.wireOp",EDGE,"E52.8"),sQuery(id+"F22.wireOp",EDGE,"E52.9"),sQuery(id+"F22.wireOp",EDGE,"E52.10"),sQuery(id+"F22.wireOp",EDGE,"E52.11")])],"isStart":true})});}
            shell(context, id + "F24", {"entities" : qUnion([Q0]), "thickness" : 2 * mm});
        }
        {
            var Q0;
            Q0=makeQuery(id+"F11.opExtrude","CAP_FACE",FACE,{"disambiguationData":[OSD([sQuery(id+"F10.wireOp",EDGE,"E27")])],"isStart":true});
            cPlane(context, id + "F25", {"entities" : qUnion([Q0]), "cplaneType" : CPlaneType.OFFSET, "offset" : 0 * mm, "width" : 150 * mm, "height" : 150 * mm});
        }
        {
            var Q0;
            Q0=qCreatedBy(id+"F25.planeOp",FACE);
            var sketch = newSketch(context, id + "F26", { "sketchPlane" : qUnion([Q0])});
            skCircle(sketch, "E57.0", {"center": v(55.94, 62.04) * mm, "radius": 1.55 * mm});
            skCircle(sketch, "E58", {"center": v(55.94, 62.04) * mm, "radius": 2.55 * mm});
            skCircle(sketch, "E59", {"center": v(55.94, 62.04) * mm, "radius": 4.05 * mm});
            skSolve(sketch);
        }
        {
            var Q0;
            Q0=makeQuery(id+"F26.imprint","IMPRINT",FACE,{"disambiguationData":[TD([[makeQuery(id+"F26.imprint","IMPRINT",EDGE,{"derivedFrom":sQuery(id+"F26.wireOp",EDGE,"278a6eca-c686-48d0-86f9-38e1a64bb2e6")}),-1.0]])]});
            var Q1;
            Q1=makeQuery(id+"F26.imprint","IMPRINT",FACE,{"disambiguationData":[TD([[makeQuery(id+"F26.imprint","IMPRINT",EDGE,{"derivedFrom":sQuery(id+"F26.wireOp",EDGE,"188b7dab-2f04-4c5b-95dc-633dce916899")}),-1.0]])]});
            var Q2;
            Q2=makeQuery(id+"F26.imprint","IMPRINT",FACE,{"disambiguationData":[TD([[makeQuery(id+"F26.imprint","IMPRINT",EDGE,{"derivedFrom":sQuery(id+"F26.wireOp",EDGE,"4327dc19-52b2-46a6-baa8-b5efde3a1f2c")}),-1.0]])]});
            var Q3;
            Q3=makeQuery(id+"F26.imprint","IMPRINT",FACE,{"disambiguationData":[TD([[makeQuery(id+"F26.imprint","IMPRINT",EDGE,{"derivedFrom":sQuery(id+"F26.wireOp",EDGE,"da1df225-7c2d-4834-b90b-7c9ac358f743")}),-1.0]])]});
            var Q4;
            Q4=makeQuery(id+"F26.imprint","IMPRINT",FACE,{"disambiguationData":[TD([[makeQuery(id+"F26.imprint","IMPRINT",EDGE,{"derivedFrom":sQuery(id+"F26.wireOp",EDGE,"17cd4f16-1c73-4021-9ff2-9c93ebed4f9e")}),-1.0]])]});
            var Q5;
            Q5=makeQuery(id+"F26.imprint","IMPRINT",FACE,{"disambiguationData":[TD([[makeQuery(id+"F26.imprint","IMPRINT",EDGE,{"derivedFrom":sQuery(id+"F26.wireOp",EDGE,"ad07df60-8bbd-455b-a9b4-e46503130f73")}),-1.0]])]});
            var Q6;
            Q6=makeQuery(id+"F26.imprint","IMPRINT",FACE,{"disambiguationData":[TD([[makeQuery(id+"F26.imprint","IMPRINT",EDGE,{"derivedFrom":sQuery(id+"F26.wireOp",EDGE,"e5b5fcf2-06c8-4c64-afef-dc603207e06b")}),-1.0]])]});
            var Q7;
            Q7=makeQuery(id+"F26.imprint","IMPRINT",FACE,{"disambiguationData":[TD([[makeQuery(id+"F26.imprint","IMPRINT",EDGE,{"derivedFrom":sQuery(id+"F26.wireOp",EDGE,"ecfa0b26-37a6-4ee3-8a9c-9deacf568bbc")}),-1.0]])]});
            var Q8;
            Q8=makeQuery(id+"F26.imprint","IMPRINT",FACE,{"disambiguationData":[TD([[makeQuery(id+"F26.imprint","IMPRINT",EDGE,{"derivedFrom":sQuery(id+"F26.wireOp",EDGE,"E58")}),-1.0]])]});
            extrude(context, id + "F27", {"entities" : qUnion([Q0, Q1, Q2, Q3, Q4, Q5, Q6, Q7, Q8]), "operationType" : NewBodyOperationType.ADD, "endBound" : BoundingType.UP_TO_NEXT, "depth" : 25 * mm});
        }
        {
            var Q0;
            Q0=makeQuery(id+"F26.imprint","IMPRINT",FACE,{"disambiguationData":[TD([[makeQuery(id+"F26.imprint","IMPRINT",EDGE,{"derivedFrom":sQuery(id+"F26.wireOp",EDGE,"54de339f-1ca7-4d6b-84b9-228a0e5b61a4.7")}),-1.0]])]});
            var Q1;
            Q1=makeQuery(id+"F26.imprint","IMPRINT",FACE,{"disambiguationData":[TD([[makeQuery(id+"F26.imprint","IMPRINT",EDGE,{"derivedFrom":sQuery(id+"F26.wireOp",EDGE,"54de339f-1ca7-4d6b-84b9-228a0e5b61a4.3")}),1.0]])]});
            var Q2;
            Q2=makeQuery(id+"F26.imprint","IMPRINT",FACE,{"disambiguationData":[TD([[makeQuery(id+"F26.imprint","IMPRINT",EDGE,{"derivedFrom":sQuery(id+"F26.wireOp",EDGE,"54de339f-1ca7-4d6b-84b9-228a0e5b61a4.3")}),-1.0]])]});
            var Q3;
            Q3=makeQuery(id+"F26.imprint","IMPRINT",FACE,{"disambiguationData":[TD([[makeQuery(id+"F26.imprint","IMPRINT",EDGE,{"derivedFrom":sQuery(id+"F26.wireOp",EDGE,"54de339f-1ca7-4d6b-84b9-228a0e5b61a4.2")}),1.0]])]});
            var Q4;
            Q4=makeQuery(id+"F26.imprint","IMPRINT",FACE,{"disambiguationData":[TD([[makeQuery(id+"F26.imprint","IMPRINT",EDGE,{"derivedFrom":sQuery(id+"F26.wireOp",EDGE,"54de339f-1ca7-4d6b-84b9-228a0e5b61a4.2")}),-1.0]])]});
            var Q5;
            Q5=makeQuery(id+"F26.imprint","IMPRINT",FACE,{"disambiguationData":[TD([[makeQuery(id+"F26.imprint","IMPRINT",EDGE,{"derivedFrom":sQuery(id+"F26.wireOp",EDGE,"54de339f-1ca7-4d6b-84b9-228a0e5b61a4.1")}),1.0]])]});
            var Q6;
            Q6=makeQuery(id+"F26.imprint","IMPRINT",FACE,{"disambiguationData":[TD([[makeQuery(id+"F26.imprint","IMPRINT",EDGE,{"derivedFrom":sQuery(id+"F26.wireOp",EDGE,"54de339f-1ca7-4d6b-84b9-228a0e5b61a4.1")}),-1.0]])]});
            var Q7;
            Q7=makeQuery(id+"F26.imprint","IMPRINT",FACE,{"disambiguationData":[TD([[makeQuery(id+"F26.imprint","IMPRINT",EDGE,{"derivedFrom":sQuery(id+"F26.wireOp",EDGE,"54de339f-1ca7-4d6b-84b9-228a0e5b61a4.0")}),1.0]])]});
            var Q8;
            Q8=makeQuery(id+"F26.imprint","IMPRINT",FACE,{"disambiguationData":[TD([[makeQuery(id+"F26.imprint","IMPRINT",EDGE,{"derivedFrom":sQuery(id+"F26.wireOp",EDGE,"54de339f-1ca7-4d6b-84b9-228a0e5b61a4.0")}),-1.0]])]});
            var Q9;
            Q9=makeQuery(id+"F26.imprint","IMPRINT",FACE,{"disambiguationData":[TD([[makeQuery(id+"F26.imprint","IMPRINT",EDGE,{"derivedFrom":sQuery(id+"F26.wireOp",EDGE,"54de339f-1ca7-4d6b-84b9-228a0e5b61a4.4")}),1.0]])]});
            var Q10;
            Q10=makeQuery(id+"F26.imprint","IMPRINT",FACE,{"disambiguationData":[TD([[makeQuery(id+"F26.imprint","IMPRINT",EDGE,{"derivedFrom":sQuery(id+"F26.wireOp",EDGE,"54de339f-1ca7-4d6b-84b9-228a0e5b61a4.4")}),-1.0]])]});
            var Q11;
            Q11=makeQuery(id+"F26.imprint","IMPRINT",FACE,{"disambiguationData":[TD([[makeQuery(id+"F26.imprint","IMPRINT",EDGE,{"derivedFrom":sQuery(id+"F26.wireOp",EDGE,"54de339f-1ca7-4d6b-84b9-228a0e5b61a4.5")}),1.0]])]});
            var Q12;
            Q12=makeQuery(id+"F26.imprint","IMPRINT",FACE,{"disambiguationData":[TD([[makeQuery(id+"F26.imprint","IMPRINT",EDGE,{"derivedFrom":sQuery(id+"F26.wireOp",EDGE,"54de339f-1ca7-4d6b-84b9-228a0e5b61a4.5")}),-1.0]])]});
            var Q13;
            Q13=makeQuery(id+"F26.imprint","IMPRINT",FACE,{"disambiguationData":[TD([[makeQuery(id+"F26.imprint","IMPRINT",EDGE,{"derivedFrom":sQuery(id+"F26.wireOp",EDGE,"54de339f-1ca7-4d6b-84b9-228a0e5b61a4.6")}),1.0]])]});
            var Q14;
            Q14=makeQuery(id+"F26.imprint","IMPRINT",FACE,{"disambiguationData":[TD([[makeQuery(id+"F26.imprint","IMPRINT",EDGE,{"derivedFrom":sQuery(id+"F26.wireOp",EDGE,"54de339f-1ca7-4d6b-84b9-228a0e5b61a4.6")}),-1.0]])]});
            var Q15;
            Q15=makeQuery(id+"F26.imprint","IMPRINT",FACE,{"disambiguationData":[TD([[makeQuery(id+"F26.imprint","IMPRINT",EDGE,{"derivedFrom":sQuery(id+"F26.wireOp",EDGE,"54de339f-1ca7-4d6b-84b9-228a0e5b61a4.6")}),-1.0]])]});
            var Q16;
            Q16=makeQuery(id+"F26.imprint","IMPRINT",FACE,{"disambiguationData":[TD([[makeQuery(id+"F26.imprint","IMPRINT",EDGE,{"derivedFrom":sQuery(id+"F26.wireOp",EDGE,"54de339f-1ca7-4d6b-84b9-228a0e5b61a4.7")}),1.0]])]});
            var Q17;
            Q17=makeQuery(id+"F26.imprint","IMPRINT",FACE,{"disambiguationData":[TD([[makeQuery(id+"F26.imprint","IMPRINT",EDGE,{"derivedFrom":sQuery(id+"F26.wireOp",EDGE,"da1df225-7c2d-4834-b90b-7c9ac358f743")}),1.0]])]});
            var Q18;
            Q18=makeQuery(id+"F26.imprint","IMPRINT",FACE,{"disambiguationData":[TD([[makeQuery(id+"F26.imprint","IMPRINT",EDGE,{"derivedFrom":sQuery(id+"F26.wireOp",EDGE,"ada74099-15d5-4d8b-96cc-69824096ed8b.1")}),1.0]])]});
            var Q19;
            Q19=makeQuery(id+"F23.opExtrude","CAP_FACE",FACE,{"disambiguationData":[OSD([sQuery(id+"F22.wireOp",EDGE,"E52.0"),sQuery(id+"F22.wireOp",EDGE,"E52.1"),sQuery(id+"F22.wireOp",EDGE,"E52.2"),sQuery(id+"F22.wireOp",EDGE,"E52.3"),sQuery(id+"F22.wireOp",EDGE,"E52.4"),sQuery(id+"F22.wireOp",EDGE,"E52.5"),sQuery(id+"F22.wireOp",EDGE,"E52.6"),sQuery(id+"F22.wireOp",EDGE,"E52.7"),sQuery(id+"F22.wireOp",EDGE,"E52.8"),sQuery(id+"F22.wireOp",EDGE,"E52.9"),sQuery(id+"F22.wireOp",EDGE,"E52.10"),sQuery(id+"F22.wireOp",EDGE,"E52.11")])],"isStart":false});
            var Q20;
            Q20=makeQuery(id+"F26.imprint","IMPRINT",FACE,{"disambiguationData":[TD([[makeQuery(id+"F26.imprint","IMPRINT",EDGE,{"derivedFrom":sQuery(id+"F26.wireOp",EDGE,"E57.0")}),-1.0]])]});
            var Q21;
            Q21=makeQuery(id+"F26.imprint","IMPRINT",FACE,{"disambiguationData":[TD([[makeQuery(id+"F26.imprint","IMPRINT",EDGE,{"derivedFrom":sQuery(id+"F26.wireOp",EDGE,"E57.0")}),1.0]])]});
            extrude(context, id + "F28", {"entities" : qUnion([Q0, Q1, Q2, Q3, Q4, Q5, Q6, Q7, Q8, Q9, Q10, Q11, Q12, Q13, Q14, Q15, Q16, Q17, Q18, Q19, Q20, Q21]), "operationType" : NewBodyOperationType.REMOVE, "depth" : 25 * mm});
        }
        {
            var Q0;
            Q0=makeQuery(id+"F26.imprint","IMPRINT",FACE,{"disambiguationData":[TD([[makeQuery(id+"F26.imprint","IMPRINT",EDGE,{"derivedFrom":sQuery(id+"F26.wireOp",EDGE,"54de339f-1ca7-4d6b-84b9-228a0e5b61a4.3")}),-1.0]])]});
            var Q1;
            Q1=makeQuery(id+"F26.imprint","IMPRINT",FACE,{"disambiguationData":[TD([[makeQuery(id+"F26.imprint","IMPRINT",EDGE,{"derivedFrom":sQuery(id+"F26.wireOp",EDGE,"54de339f-1ca7-4d6b-84b9-228a0e5b61a4.2")}),-1.0]])]});
            var Q2;
            Q2=makeQuery(id+"F26.imprint","IMPRINT",FACE,{"disambiguationData":[TD([[makeQuery(id+"F26.imprint","IMPRINT",EDGE,{"derivedFrom":sQuery(id+"F26.wireOp",EDGE,"54de339f-1ca7-4d6b-84b9-228a0e5b61a4.1")}),-1.0]])]});
            var Q3;
            Q3=makeQuery(id+"F26.imprint","IMPRINT",FACE,{"disambiguationData":[TD([[makeQuery(id+"F26.imprint","IMPRINT",EDGE,{"derivedFrom":sQuery(id+"F26.wireOp",EDGE,"54de339f-1ca7-4d6b-84b9-228a0e5b61a4.0")}),-1.0]])]});
            var Q4;
            Q4=makeQuery(id+"F26.imprint","IMPRINT",FACE,{"disambiguationData":[TD([[makeQuery(id+"F26.imprint","IMPRINT",EDGE,{"derivedFrom":sQuery(id+"F26.wireOp",EDGE,"54de339f-1ca7-4d6b-84b9-228a0e5b61a4.4")}),-1.0]])]});
            var Q5;
            Q5=makeQuery(id+"F26.imprint","IMPRINT",FACE,{"disambiguationData":[TD([[makeQuery(id+"F26.imprint","IMPRINT",EDGE,{"derivedFrom":sQuery(id+"F26.wireOp",EDGE,"54de339f-1ca7-4d6b-84b9-228a0e5b61a4.5")}),-1.0]])]});
            var Q6;
            Q6=makeQuery(id+"F26.imprint","IMPRINT",FACE,{"disambiguationData":[TD([[makeQuery(id+"F26.imprint","IMPRINT",EDGE,{"derivedFrom":sQuery(id+"F26.wireOp",EDGE,"54de339f-1ca7-4d6b-84b9-228a0e5b61a4.6")}),-1.0]])]});
            var Q7;
            Q7=makeQuery(id+"F26.imprint","IMPRINT",FACE,{"disambiguationData":[TD([[makeQuery(id+"F26.imprint","IMPRINT",EDGE,{"derivedFrom":sQuery(id+"F26.wireOp",EDGE,"54de339f-1ca7-4d6b-84b9-228a0e5b61a4.7")}),-1.0]])]});
            var Q8;
            Q8=makeQuery(id+"F26.imprint","IMPRINT",FACE,{"disambiguationData":[TD([[makeQuery(id+"F26.imprint","IMPRINT",EDGE,{"derivedFrom":sQuery(id+"F26.wireOp",EDGE,"da1df225-7c2d-4834-b90b-7c9ac358f743")}),1.0]])]});
            var Q9;
            Q9=makeQuery(id+"F26.imprint","IMPRINT",FACE,{"disambiguationData":[TD([[makeQuery(id+"F26.imprint","IMPRINT",EDGE,{"derivedFrom":sQuery(id+"F26.wireOp",EDGE,"E57.0")}),-1.0]])]});
            extrude(context, id + "F29", {"entities" : qUnion([Q0, Q1, Q2, Q3, Q4, Q5, Q6, Q7, Q8, Q9]), "operationType" : NewBodyOperationType.ADD, "depth" : 1.27 * mm});
        }
        {
            var Q0;
            Q0=makeQuery(id+"F23.opExtrude","CAP_FACE",FACE,{"disambiguationData":[OSD([sQuery(id+"F22.wireOp",EDGE,"E52.0"),sQuery(id+"F22.wireOp",EDGE,"E52.1"),sQuery(id+"F22.wireOp",EDGE,"E52.2"),sQuery(id+"F22.wireOp",EDGE,"E52.3"),sQuery(id+"F22.wireOp",EDGE,"E52.4"),sQuery(id+"F22.wireOp",EDGE,"E52.5"),sQuery(id+"F22.wireOp",EDGE,"E52.6"),sQuery(id+"F22.wireOp",EDGE,"E52.7"),sQuery(id+"F22.wireOp",EDGE,"E52.8"),sQuery(id+"F22.wireOp",EDGE,"E52.9"),sQuery(id+"F22.wireOp",EDGE,"E52.10"),sQuery(id+"F22.wireOp",EDGE,"E52.11")])],"isStart":false});
            var sketch = newSketch(context, id + "F30", { "sketchPlane" : qUnion([Q0])});
            skCircle(sketch, "E60.0", {"center": v(-33.03, 106.98) * mm, "radius": 1.55 * mm, "construction": true});
            skLineSegment(sketch, "E61.bottom", {"start": v(-27.03, 102.48) * mm, "end": v(-15.03, 102.48) * mm});
            skLineSegment(sketch, "E61.top", {"start": v(-27.03, 91.48) * mm, "end": v(-15.03, 91.48) * mm});
            skLineSegment(sketch, "E61.left", {"start": v(-27.03, 102.48) * mm, "end": v(-27.03, 91.48) * mm});
            skLineSegment(sketch, "E61.right", {"start": v(-15.03, 102.48) * mm, "end": v(-15.03, 91.48) * mm});
            skLineSegment(sketch, "E62.1.0.0", {"start": v(-26.85, 79.73) * mm, "end": v(-26.85, 68.73) * mm});
            skLineSegment(sketch, "E62.1.0.1", {"start": v(-26.85, 79.73) * mm, "end": v(-14.85, 79.73) * mm});
            skLineSegment(sketch, "E62.1.0.2", {"start": v(-14.85, 79.73) * mm, "end": v(-14.85, 68.73) * mm});
            skLineSegment(sketch, "E62.1.0.3", {"start": v(-26.85, 68.73) * mm, "end": v(-14.85, 68.73) * mm});
            skLineSegment(sketch, "E62.2.0.0", {"start": v(-26.66, 56.98) * mm, "end": v(-26.66, 45.98) * mm});
            skLineSegment(sketch, "E62.2.0.1", {"start": v(-26.66, 56.98) * mm, "end": v(-14.66, 56.98) * mm});
            skLineSegment(sketch, "E62.2.0.2", {"start": v(-14.66, 56.98) * mm, "end": v(-14.66, 45.98) * mm});
            skLineSegment(sketch, "E62.2.0.3", {"start": v(-26.66, 45.98) * mm, "end": v(-14.66, 45.98) * mm});
            skLineSegment(sketch, "E62.3.0.0", {"start": v(-26.48, 34.23) * mm, "end": v(-26.48, 23.23) * mm});
            skLineSegment(sketch, "E62.3.0.1", {"start": v(-26.48, 34.23) * mm, "end": v(-14.48, 34.23) * mm});
            skLineSegment(sketch, "E62.3.0.2", {"start": v(-14.48, 34.23) * mm, "end": v(-14.48, 23.23) * mm});
            skLineSegment(sketch, "E62.3.0.3", {"start": v(-26.48, 23.23) * mm, "end": v(-14.48, 23.23) * mm});
            skLineSegment(sketch, "E62.4.0.0", {"start": v(-26.3, 11.48) * mm, "end": v(-26.3, 0.48) * mm});
            skLineSegment(sketch, "E62.4.0.1", {"start": v(-26.3, 11.48) * mm, "end": v(-14.3, 11.48) * mm});
            skLineSegment(sketch, "E62.4.0.2", {"start": v(-14.3, 11.48) * mm, "end": v(-14.3, 0.48) * mm});
            skLineSegment(sketch, "E62.4.0.3", {"start": v(-26.3, 0.48) * mm, "end": v(-14.3, 0.48) * mm});
            skLineSegment(sketch, "E62.direction1", {"start": v(-27.03, 91.48) * mm, "end": v(-26.85, 68.73) * mm, "construction": true});
            skLineSegment(sketch, "E63.bottom", {"start": v(-26.28, -43.02) * mm, "end": v(-15.28, -43.02) * mm});
            skLineSegment(sketch, "E63.top", {"start": v(-26.28, -31.02) * mm, "end": v(-15.28, -31.02) * mm});
            skLineSegment(sketch, "E63.left", {"start": v(-26.28, -43.02) * mm, "end": v(-26.28, -31.02) * mm});
            skLineSegment(sketch, "E63.right", {"start": v(-15.28, -43.02) * mm, "end": v(-15.28, -31.02) * mm});
            skLineSegment(sketch, "E64.bottom", {"start": v(94.14, 23.7) * mm, "end": v(97.97, 23.7) * mm});
            skLineSegment(sketch, "E64.top", {"start": v(94.14, 14.28) * mm, "end": v(97.97, 14.28) * mm});
            skLineSegment(sketch, "E64.left", {"start": v(94.14, 23.7) * mm, "end": v(94.14, 14.28) * mm});
            skLineSegment(sketch, "E64.right", {"start": v(97.97, 23.7) * mm, "end": v(97.97, 14.28) * mm});
            skLineSegment(sketch, "E65.bottom", {"start": v(77.97, 25.23) * mm, "end": v(89.97, 25.23) * mm});
            skLineSegment(sketch, "E65.top", {"start": v(77.97, 51.23) * mm, "end": v(89.97, 51.23) * mm});
            skLineSegment(sketch, "E65.left", {"start": v(77.97, 25.23) * mm, "end": v(77.97, 51.23) * mm});
            skLineSegment(sketch, "E65.right", {"start": v(89.97, 25.23) * mm, "end": v(89.97, 51.23) * mm});
            skLineSegment(sketch, "E66.bottom", {"start": v(77.97, 57.23) * mm, "end": v(89.97, 57.23) * mm});
            skLineSegment(sketch, "E66.top", {"start": v(77.97, 83.23) * mm, "end": v(89.97, 83.23) * mm});
            skLineSegment(sketch, "E66.left", {"start": v(77.97, 57.23) * mm, "end": v(77.97, 83.23) * mm});
            skLineSegment(sketch, "E66.right", {"start": v(89.97, 57.23) * mm, "end": v(89.97, 83.23) * mm});
            skLineSegment(sketch, "E67.bottom", {"start": v(77.97, 85.48) * mm, "end": v(89.97, 85.48) * mm});
            skLineSegment(sketch, "E67.top", {"start": v(77.97, 105.98) * mm, "end": v(89.97, 105.98) * mm});
            skLineSegment(sketch, "E67.left", {"start": v(77.97, 85.48) * mm, "end": v(77.97, 105.98) * mm});
            skLineSegment(sketch, "E67.right", {"start": v(89.97, 85.48) * mm, "end": v(89.97, 105.98) * mm});
            skLineSegment(sketch, "E68.0", {"start": v(-39.03, 115.98) * mm, "end": v(94.97, 115.98) * mm, "construction": true});
            skLineSegment(sketch, "E69.0", {"start": v(-40.03, -40.02) * mm, "end": v(-40.03, 113.98) * mm, "construction": true});
            skLineSegment(sketch, "E70.0", {"start": v(95.97, 113.98) * mm, "end": v(95.97, 4.98) * mm, "construction": true});
            skLineSegment(sketch, "E71.bottom", {"start": v(-9.03, 79.98) * mm, "end": v(0.97, 79.98) * mm});
            skLineSegment(sketch, "E71.top", {"start": v(-9.03, 64.98) * mm, "end": v(0.97, 64.98) * mm});
            skLineSegment(sketch, "E71.left", {"start": v(-9.03, 79.98) * mm, "end": v(-9.03, 64.98) * mm});
            skLineSegment(sketch, "E71.right", {"start": v(0.97, 79.98) * mm, "end": v(0.97, 64.98) * mm});
            skSolve(sketch);
        }
        {
            var Q0;
            Q0=qSketchRegion(id+"F30",true);
            extrude(context, id + "F31", {"entities" : qUnion([Q0]), "operationType" : NewBodyOperationType.REMOVE, "oppositeDirection" : true, "depth" : getVariable(context, 'TopShellHeight') + 4 * mm});
        }
        {
            var Q0;
            {var subQ0=sQuery(id+"F13.wireOp",EDGE,"E36.5.left");var subQ1=makeQuery(id+"F14.opExtrude","CAP_EDGE",EDGE,{"disambiguationData":[OSD([subQ0]),TDD([makeQuery(id+"F13.imprint","IMPRINT",EDGE,{"disambiguationData":[TD([[makeQuery(id+"F13.imprint","INTERSECT",VERTEX,{"derivedFrom":[sQuery(id+"F13.wireOp",EDGE,"E36.5.startCap"),subQ0]}),-1.0]])],"derivedFrom":subQ0})])],"isStart":false});var subQ2=sQuery(id+"F7.wireOp",EDGE,"E15");var subQ6=makeQuery(id+"F7.imprint","INTERSECT",VERTEX,{"disambiguationData":[OD(0.0)],"derivedFrom":[subQ1,subQ2]});Q0=makeQuery(id+"F7.imprint","IMPRINT",FACE,{"disambiguationData":[TD([[makeQuery(id+"F7.imprint","IMPRINT",EDGE,{"disambiguationData":[TD([[subQ6,-1.0]])],"derivedFrom":subQ2}),-1.0]])]});}
            var Q1;
            Q1=makeQuery(id+"F7.imprint","IMPRINT",FACE,{"disambiguationData":[TD([[makeQuery(id+"F7.imprint","IMPRINT",EDGE,{"derivedFrom":sQuery(id+"F7.wireOp",EDGE,"E13")}),-1.0]])]});
            var Q2;
            Q2=makeQuery(id+"F7.imprint","IMPRINT",FACE,{"disambiguationData":[TD([[makeQuery(id+"F7.imprint","IMPRINT",EDGE,{"derivedFrom":sQuery(id+"F7.wireOp",EDGE,"E14")}),-1.0]])]});
            extrude(context, id + "F32", {"entities" : qUnion([Q0, Q1, Q2]), "operationType" : NewBodyOperationType.ADD, "depth" : 2 * mm});
        }
        {
            var Q0;
            Q0=sQuery(id+"F7.wireOp",VERTEX,"E19.rect.right.end");
            var Q1;
            Q1=sQuery(id+"F7.wireOp",VERTEX,"E19.rect.left.end");
            var Q2;
            Q2=sQuery(id+"F7.wireOp",VERTEX,"E19.rect.left.start");
            var Q3;
            Q3=sQuery(id+"F7.wireOp",VERTEX,"E19.rect.right.start");
            var Q4;
            Q4=makeQuery(id+"F4.opExtrude","SWEPT_BODY",BODY,{"disambiguationData":[OSD([sQuery(id+"F3.wireOp",EDGE,"E0"),sQuery(id+"F3.wireOp",EDGE,"E1"),sQuery(id+"F3.wireOp",EDGE,"E2"),sQuery(id+"F3.wireOp",EDGE,"E3"),sQuery(id+"F3.wireOp",EDGE,"E4"),sQuery(id+"F3.wireOp",EDGE,"E5")])]});
            hole(context, id + "F33", {"style" : HoleStyle.SIMPLE, "holeDiameter" : 4 * mm, "endStyle" : HoleEndStyle.THROUGH, "locations" : qUnion([Q0, Q1, Q2, Q3]), "scope" : qUnion([Q4])});
        }
        {
            var Q0;
            Q0=makeQuery(id+"F23.opExtrude","SWEPT_FACE",FACE,{"disambiguationData":[OSD([sQuery(id+"F22.wireOp",EDGE,"E56")])]});
            var sketch = newSketch(context, id + "F34", { "sketchPlane" : qUnion([Q0])});
            skLineSegment(sketch, "E72.0", {"start": v(-103.98, 40) * mm, "end": v(-103.98, 17) * mm, "construction": true});
            skLineSegment(sketch, "E73.bottom", {"start": v(-103.98, 30) * mm, "end": v(8.02, 30) * mm});
            skLineSegment(sketch, "E73.top", {"start": v(-103.98, 15) * mm, "end": v(8.02, 15) * mm});
            skLineSegment(sketch, "E73.left", {"start": v(-103.98, 30) * mm, "end": v(-103.98, 15) * mm});
            skLineSegment(sketch, "E73.right", {"start": v(8.02, 30) * mm, "end": v(8.02, 15) * mm});
            skLineSegment(sketch, "E74.bottom", {"start": v(-31.98, 10) * mm, "end": v(8.02, 10) * mm});
            skLineSegment(sketch, "E74.top", {"start": v(-31.98, 15) * mm, "end": v(8.02, 15) * mm});
            skLineSegment(sketch, "E74.left", {"start": v(-31.98, 10) * mm, "end": v(-31.98, 15) * mm});
            skLineSegment(sketch, "E74.right", {"start": v(8.02, 10) * mm, "end": v(8.02, 15) * mm});
            skSolve(sketch);
        }
        {
            var Q0;
            Q0=qSketchRegion(id+"F34",true);
            extrude(context, id + "F35", {"entities" : qUnion([Q0]), "operationType" : NewBodyOperationType.REMOVE, "oppositeDirection" : true, "depth" : 25 * mm});
        }
        {
            var Q0;
            Q0=makeQuery(id+"F35.boolean.opBoolean","COPY",EDGE,{"derivedFrom":makeQuery(id+"F35.opExtrude","SWEPT_EDGE",EDGE,{"disambiguationData":[OSD([sQuery(id+"F34.wireOp",EDGE,"E73.top"),sQuery(id+"F34.wireOp",EDGE,"E74.top"),sQuery(id+"F34.wireOp",EDGE,"E74.left")])]})});
            var Q1;
            Q1=makeQuery(id+"F35.boolean.opBoolean","COPY",EDGE,{"derivedFrom":makeQuery(id+"F35.opExtrude","SWEPT_EDGE",EDGE,{"disambiguationData":[OSD([sQuery(id+"F34.wireOp",EDGE,"E74.bottom"),sQuery(id+"F34.wireOp",EDGE,"E74.left")])]})});
            var Q2;
            Q2=makeQuery(id+"F35.boolean.opBoolean","COPY",EDGE,{"derivedFrom":makeQuery(id+"F35.opExtrude","SWEPT_EDGE",EDGE,{"disambiguationData":[OSD([sQuery(id+"F34.wireOp",EDGE,"E74.bottom"),sQuery(id+"F34.wireOp",EDGE,"E74.right")])]})});
            fillet(context, id + "F36", {"entities" : qUnion([Q0, Q1, Q2]), "radius" : 2 * mm, "tangentPropagation" : true, "allowEdgeOverflow" : false});
        }
    });
